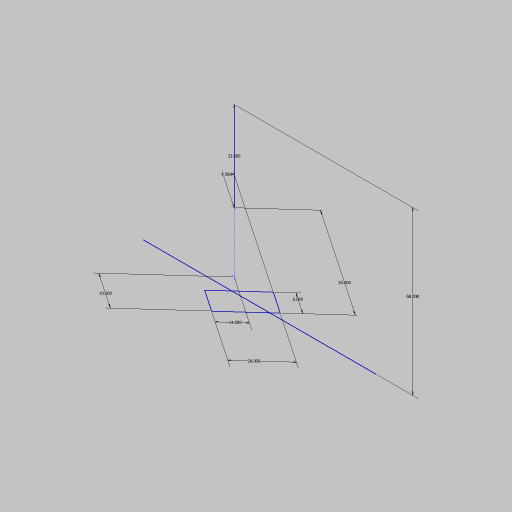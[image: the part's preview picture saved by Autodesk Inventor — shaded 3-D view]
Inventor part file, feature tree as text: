
AUTODESK INVENTOR PART (.ipt)
format: ipt  version: 2023.5 (Build 275446000, 446)  size: 80,384 bytes
history: native  units: in
note: dims shown in document units (in); Inventor stores cm internally (conversion verified against a paired STEP export)
features: sketch x1
ambient origin geometry x8: Origin, YZ Plane, XZ Plane, XY Plane, X Axis, Y Axis, Z Axis, Center Point
feature tree (1):
  sketch  "Sketch1"  dims[d0=33.0in d1=60.0in d2=14.0in d3=10.0in d4=6.0in d5=28.0in d6=30.0in d7=4.5in]
